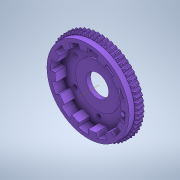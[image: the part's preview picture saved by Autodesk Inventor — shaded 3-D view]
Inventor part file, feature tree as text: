
AUTODESK INVENTOR PART (.ipt)
format: ipt  version: 2022.1 (Build 261234000, 234)  size: 1,401,856 bytes
history: native  units: mm (DEFAULTED — no unit token found)
features: other x21, sketch x9, extrude x7, plane x4, pattern_circular x2, split x1, hole x1, projected_geometry x1
ambient origin geometry x5: Origin, X Axis, Y Axis, Z Axis, Center Point
bodies: Solid1 (feature_tree)
feature tree (46):
  other  "Annotations"
  other  "Tooth Plane"
  other  "Base Body Sketch"
  other  "Base Body"
  other  "Base Body2"
  plane  "Work Plane13"
  other  "Tooth"
  pattern_circular  "Tooth Pattern"  Count=60  [1 undecoded]
  plane  "Work Plane14"
  plane  "Work Plane15"
  extrude  "Extrusion2"  Depth=9.525mm
  extrude  "Extrusion3"  Depth=9.525mm
  extrude  "Extrusion7"  Depth=9.525mm TaperAngle=0.0deg
  pattern_circular  "Circular Pattern7"  [2 undecoded]
  extrude  "Extrusion8"  Depth=9.525mm
  extrude  "Extrusion9"  TaperAngle=0.0deg  [1 undecoded]
  extrude  "Extrusion10"  Depth=9.525mm TaperAngle=0.0deg
  plane  "Work Plane18"
  split  "Split2"
  hole  "Hole3"  [1 undecoded]
  extrude  "Extrusion11"  Depth=9.525mm
  other  "Tooth Sketch"
  sketch  "Sketch8"  dims[d35=90.0deg]
  other  "Srf1"
  sketch  "Sketch10"  dims[d37=-0.996687mm]
  sketch  "Sketch11"  dims[d38=56.595498mm]
  sketch  "Sketch16"  dims[d39=3.490659mm]
  other  "Work Axis2"
  other  "Work Axis3"
  other  "Work Axis4"
  other  "Work Axis5"
  other  "Work Axis6"
  other  "Work Axis7"
  other  "Work Axis8"
  other  "Work Axis9"
  other  "Work Axis10"
  other  "Work Axis11"
  other  "Work Axis12"
  sketch  "Sketch17"  dims[d40=6.144654mm]
  sketch  "Sketch18"  dims[d41=8.085071mm]
  sketch  "Sketch19"  dims[d42=1.524mm]
  sketch  "Sketch20"  dims[d43=90.0deg d44=600.0mm]
  sketch  "Sketch21"  dims[d46=360.0deg d50=5.130925mm d68=56.595498mm d69=0.0mm d73=0.0mm d75=0.523599mm d77=97.020853mm d78=9.525mm d79=0.0mm d80=0.0mm d81=0.0mm d82=0.0mm d83=0.523599mm d84=0.0mm d85=180.0deg d86=56.595498mm d87=101.871896mm d89=12.936114mm d90=90.0deg d92=9.525mm d93=56.595498mm d97=76.3905mm d98=0.0mm d99=0.0mm d102=25.781mm d103=94.869mm d104=6.35mm d105=0.0mm d151=0.087266mm d152=2.792527mm d153=5.177778mm d154=9.525mm d155=0.0mm d156=120.0mm d157=360.0deg d159=76.3905mm d160=86.746057mm d168=50.8mm d169=4.7625mm d170=0.0mm d171=88.9mm d172=5.08mm d173=5.08mm d174=2.54mm d175=0.0mm d180=3.175mm d181=0.0mm d185=0.0mm d186=31.75mm d187=60.0mm d189=360.0deg d191=4.9149mm d192=19.05mm d193=14.2875mm d194=3.048mm d195=14.3117mm d196=25.4mm d197=20.594885mm d198=6.35mm d199=0.0mm d177=7.715547mm d178=7.103274mm d179=9.525mm]
  projected_geometry  "Projected Loop1"
  other  "Pitch Diameter"
  other  "Linear Dimension 2"
note: 5 required parameter values undecoded (feature->parameter linkage not recoverable at this tier; creation-order binding heuristic only, values carry confidence <= 0.55)
